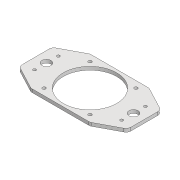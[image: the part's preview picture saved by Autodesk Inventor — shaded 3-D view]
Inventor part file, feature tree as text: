
AUTODESK INVENTOR PART (.ipt)
format: ipt  version: 2020 (Build 240168000, 168)  size: 148,992 bytes
history: native  units: mm
features: mirror x2, other x1, extrude x1
ambient origin geometry x8: Origin, YZ Plane, XZ Plane, XY Plane, X Axis, Y Axis, Z Axis, Center Point
bodies: Body1 (feature_tree)
feature tree (4):
  other  "Sólido1"
  extrude  "Extrusão1"  Depth=65.0mm
  mirror  "Espelhamento1"
  mirror  "Espelhamento3"
